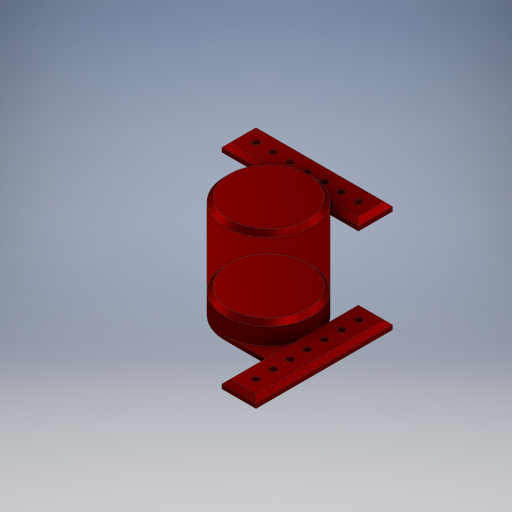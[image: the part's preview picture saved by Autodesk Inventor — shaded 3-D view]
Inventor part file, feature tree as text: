
AUTODESK INVENTOR PART (.ipt)
format: ipt  version: 2024.2 (Build 282272000, 272)  size: 456,704 bytes
history: native  units: in
note: dims shown in document units (in); Inventor stores cm internally (conversion verified against a paired STEP export)
features: projected_geometry x8, extrude x6, sketch x6, chamfer x2
ambient origin geometry x8: Origin, YZ Plane, XZ Plane, XY Plane, X Axis, Y Axis, Z Axis, Center Point
bodies: Solid1 (feature_tree)
feature tree (22):
  extrude  "Extrusion1"  Depth=2.3in
  extrude  "Extrusion2"  Depth=2.263in
  extrude  "Extrusion3"  Depth=0.125in
  chamfer  "Chamfer1"  Distance=0.586in
  extrude  "Extrusion4"  Depth=0.125in TaperAngle=0.0deg
  chamfer  "Chamfer2"  Distance=0.125in Angle=45.0deg
  extrude  "Extrusion5"  Depth=1.448in
  extrude  "Extrusion6"  Depth=1.0in
  sketch  "Sketch1"  dims[d0=2.3in d1=2.3in]
  sketch  "Sketch2"  dims[d2=2.263in d3=2.263in]
  projected_geometry  "Projected Loop1"
  projected_geometry  "Projected Loop2"
  sketch  "Sketch3"  dims[d4=0.125in d5=0.125in d6=0.586in d7=0.0in]
  projected_geometry  "Projected Loop3"
  projected_geometry  "Projected Loop4"
  sketch  "Sketch4"  dims[d8=0.03in d9=0.0in d10=0.125in d11=0.0in d12=0.125in d13=0.125in d14=45.0deg]
  projected_geometry  "Projected Loop5"
  sketch  "Sketch5"  dims[d16=2.185in d18=1.448in]
  projected_geometry  "Projected Loop6"
  projected_geometry  "Projected Loop7"
  sketch  "Sketch6"  dims[d19=2.185in d20=1.0in d21=4.0in d26=1.448in d27=2.185in d28=1.0in d29=4.0in d30=0.196in d31=0.5in d32=0.5in d33=2.7559in d35=0.5in d36=0.3937in d38=1.0in d40=0.196in d41=0.5in d42=0.5in d43=2.7559in d45=0.5in d46=0.3937in d48=1.0in d50=0.25in d51=0.0in d52=0.125in d53=0.125in d54=45.0deg d55=0.616in d56=0.0in d57=0.125in d58=0.0in]
  projected_geometry  "Projected Loop8"
